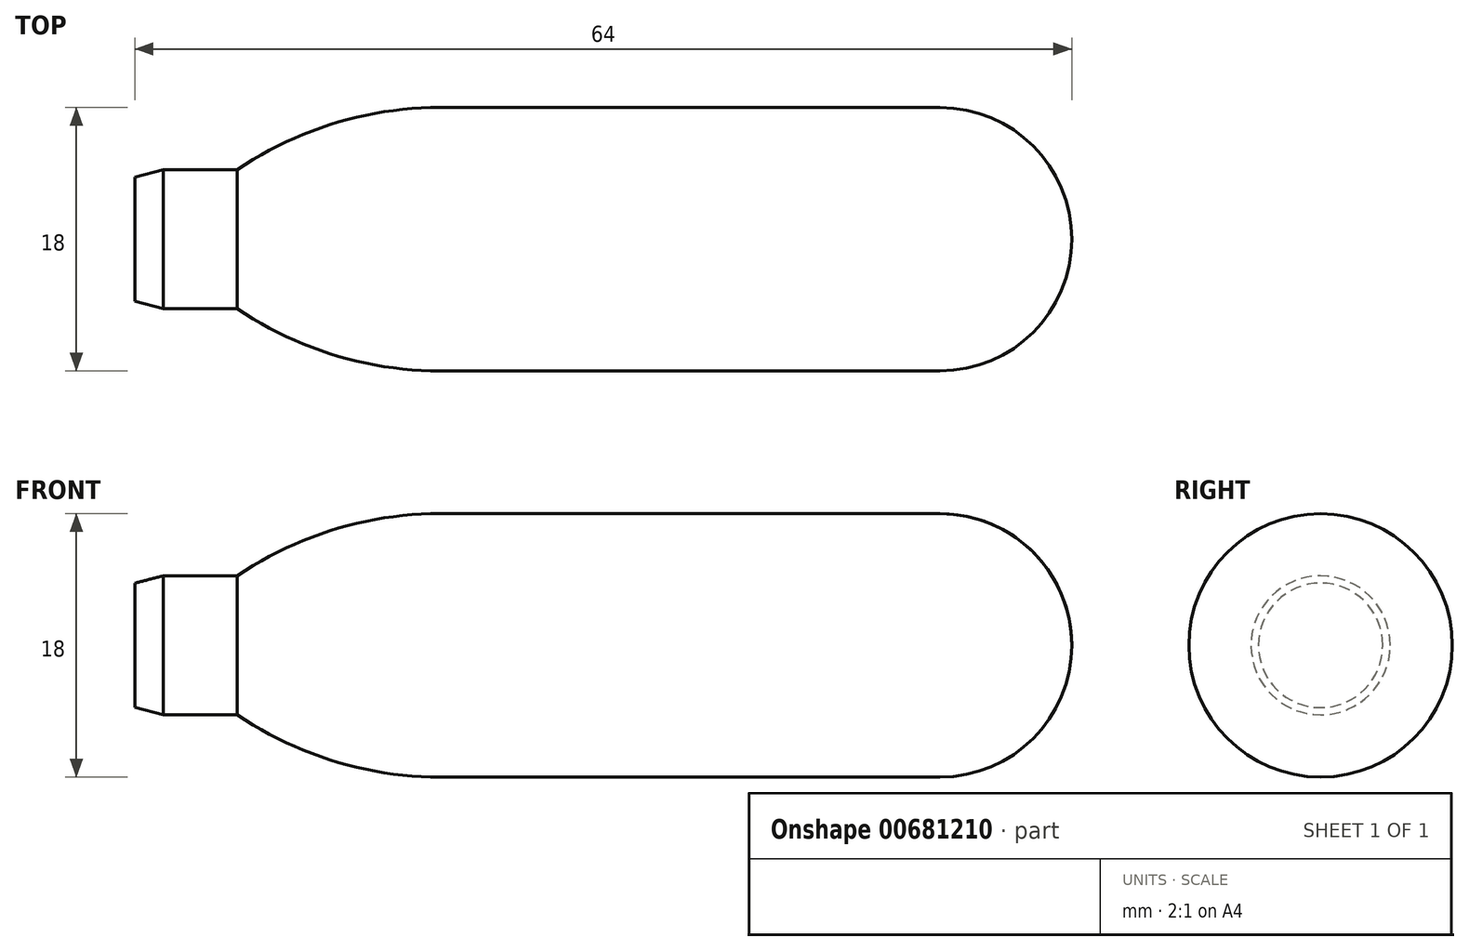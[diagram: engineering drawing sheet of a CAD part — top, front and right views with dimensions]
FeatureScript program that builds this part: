
annotation { "Feature Type Name" : "Feature", "Feature Type Description" : "" }
export const myFeature = defineFeature(function(context is Context, id is Id, definition is map)
    precondition{}
    {
        {
            var Q0;
            Q0=qCreatedBy(makeId("Front.planeOp"),FACE);
            var sketch = newSketch(context, id + "F0", { "sketchPlane" : qUnion([Q0])});
            skLineSegment(sketch, "E0", {"start": v(0, 0) * mm, "end": v(0, 4.25) * mm});
            skLineSegment(sketch, "E1", {"start": v(0, 0) * mm, "end": v(64, 0) * mm});
            skLineSegment(sketch, "E2", {"start": v(64, 0) * mm, "end": v(64, 9) * mm});
            skLineSegment(sketch, "E3", {"start": v(0, 4.25) * mm, "end": v(1.94, 4.75) * mm});
            skLineSegment(sketch, "E4", {"start": v(1.94, 4.75) * mm, "end": v(7, 4.75) * mm});
            skLineSegment(sketch, "E5", {"start": v(64, 9) * mm, "end": v(20.85, 9) * mm});
            skArc(sketch, "E6", {"start": v(20.85, 9) * mm, "mid": v(13.6, 7.91) * mm, "end": v(7, 4.75) * mm});
            skSolve(sketch);
        }
        {
            var Q0;
            Q0=makeQuery(id+"F0.imprint","IMPRINT",FACE,{"disambiguationData":[TD([[makeQuery(id+"F0.imprint","IMPRINT",EDGE,{"derivedFrom":sQuery(id+"F0.wireOp",EDGE,"E0")}),-1.0]])]});
            var Q1;
            Q1=sQuery(id+"F0.wireOp",EDGE,"E1");
            revolve(context, id + "F1", {"entities" : qUnion([Q0]), "axis" : qUnion([Q1]), "revolveType" : RevolveType.FULL});
        }
        {
            var Q0;
            Q0=makeQuery(id+"F1.opRevolve","SWEPT_EDGE",EDGE,{"disambiguationData":[OSD([sQuery(id+"F0.wireOp",EDGE,"E2"),sQuery(id+"F0.wireOp",EDGE,"E5")])]});
            fillet(context, id + "F2", {"entities" : qUnion([Q0]), "radius" : 9 * mm, "tangentPropagation" : true, "allowEdgeOverflow" : false});
        }
    });
